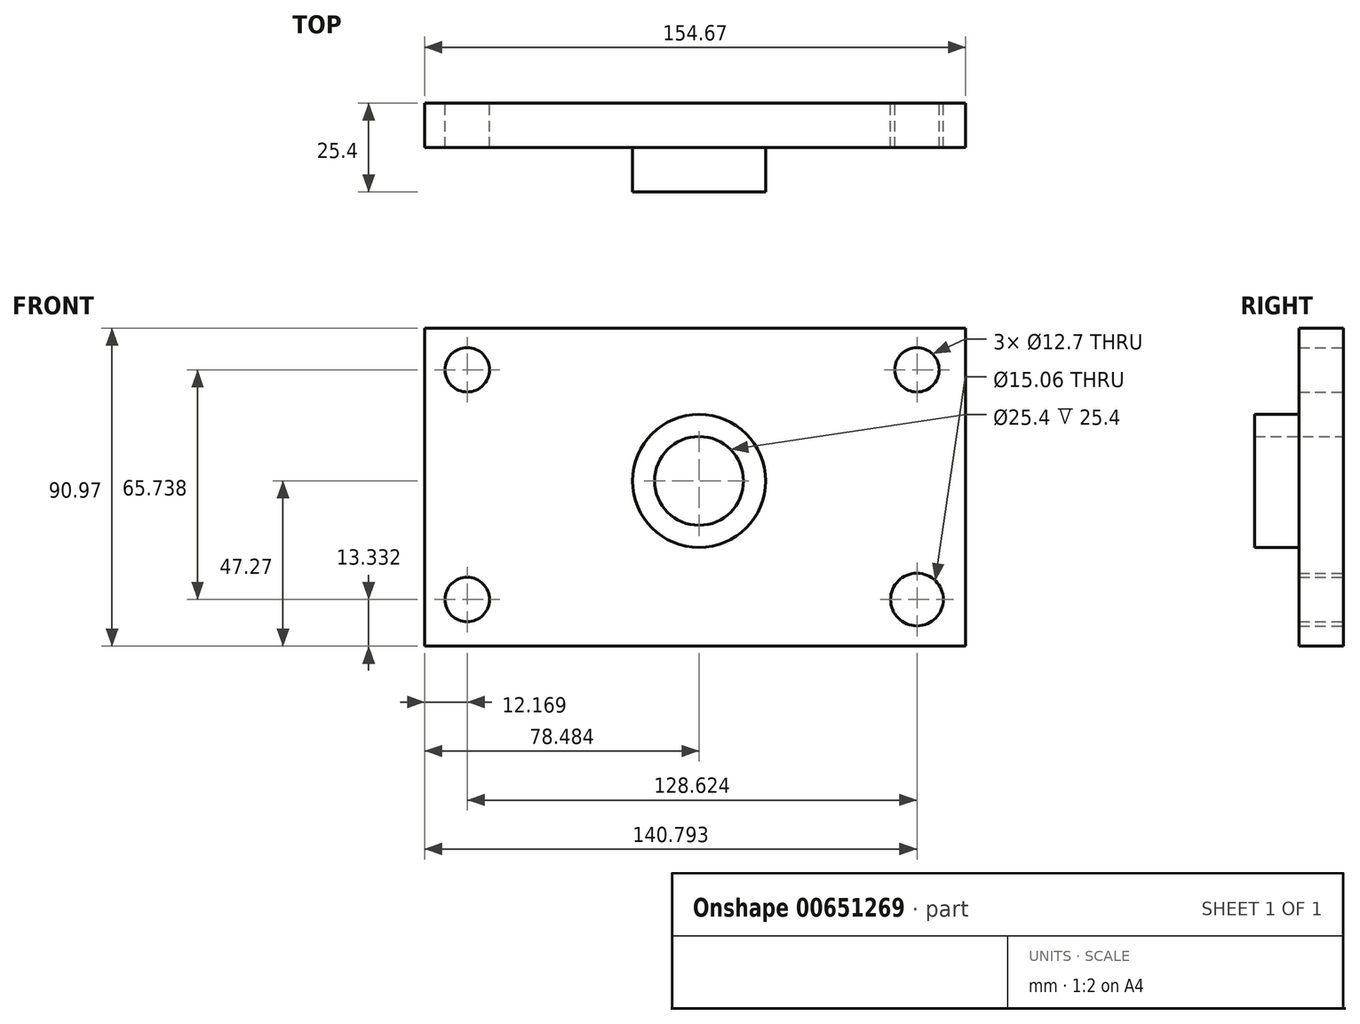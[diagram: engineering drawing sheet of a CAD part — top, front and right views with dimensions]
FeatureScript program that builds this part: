
annotation { "Feature Type Name" : "Feature", "Feature Type Description" : "" }
export const myFeature = defineFeature(function(context is Context, id is Id, definition is map)
    precondition{}
    {
        {
            var Q0;
            Q0=qCreatedBy(makeId("Front.planeOp"),FACE);
            var sketch = newSketch(context, id + "F0", { "sketchPlane" : qUnion([Q0])});
            skLineSegment(sketch, "E0.bottom", {"start": v(-97.34, 43.7) * mm, "end": v(57.33, 43.7) * mm});
            skLineSegment(sketch, "E0.top", {"start": v(-97.34, -47.27) * mm, "end": v(57.33, -47.27) * mm});
            skLineSegment(sketch, "E0.left", {"start": v(-97.34, 43.7) * mm, "end": v(-97.34, -47.27) * mm});
            skLineSegment(sketch, "E0.right", {"start": v(57.33, 43.7) * mm, "end": v(57.33, -47.27) * mm});
            skCircle(sketch, "E1", {"center": v(-18.86, 0) * mm, "radius": 19.05 * mm});
            skCircle(sketch, "E2", {"center": v(-85.17, 31.8) * mm, "radius": 6.35 * mm});
            skCircle(sketch, "E3", {"center": v(-85.17, -33.94) * mm, "radius": 6.35 * mm});
            skCircle(sketch, "E4", {"center": v(43.45, -33.94) * mm, "radius": 7.53 * mm});
            skCircle(sketch, "E5", {"center": v(43.45, 31.8) * mm, "radius": 6.35 * mm});
            skSolve(sketch);
        }
        {
            var Q0;
            Q0=makeQuery(id+"F0.imprint","IMPRINT",FACE,{"disambiguationData":[TD([[makeQuery(id+"F0.imprint","IMPRINT",EDGE,{"derivedFrom":sQuery(id+"F0.wireOp",EDGE,"E1")}),1.0]])]});
            extrude(context, id + "F1", {"entities" : qUnion([Q0]), "depth" : 25.4 * mm, "offsetDistance" : 25.4 * mm});
        }
        {
            var Q0;
            Q0=makeQuery(id+"F0.imprint","IMPRINT",FACE,{"disambiguationData":[TD([[makeQuery(id+"F0.imprint","IMPRINT",EDGE,{"derivedFrom":sQuery(id+"F0.wireOp",EDGE,"E0.bottom")}),-1.0]])]});
            extrude(context, id + "F2", {"entities" : qUnion([Q0]), "operationType" : NewBodyOperationType.ADD, "depth" : 12.7 * mm, "offsetDistance" : 25.4 * mm});
        }
        {
            var Q0;
            Q0=sQuery(id+"F0.wireOp",VERTEX,"E1.center");
            var Q1;
            Q1=makeQuery(id+"F1.opExtrude","SWEPT_BODY",BODY,{"disambiguationData":[OSD([sQuery(id+"F0.wireOp",EDGE,"E1")])]});
            hole(context, id + "F3", {"style" : HoleStyle.SIMPLE, "endStyle" : HoleEndStyle.THROUGH, "oppositeDirection" : true, "holeDiameter" : 25.4 * mm, "majorDiameter" : 6.35 * mm, "isTappedThrough" : true, "tappedDepth" : 12.7 * mm, "tapClearance" : 3, "locations" : qUnion([Q0]), "scope" : qUnion([Q1])});
        }
    });
